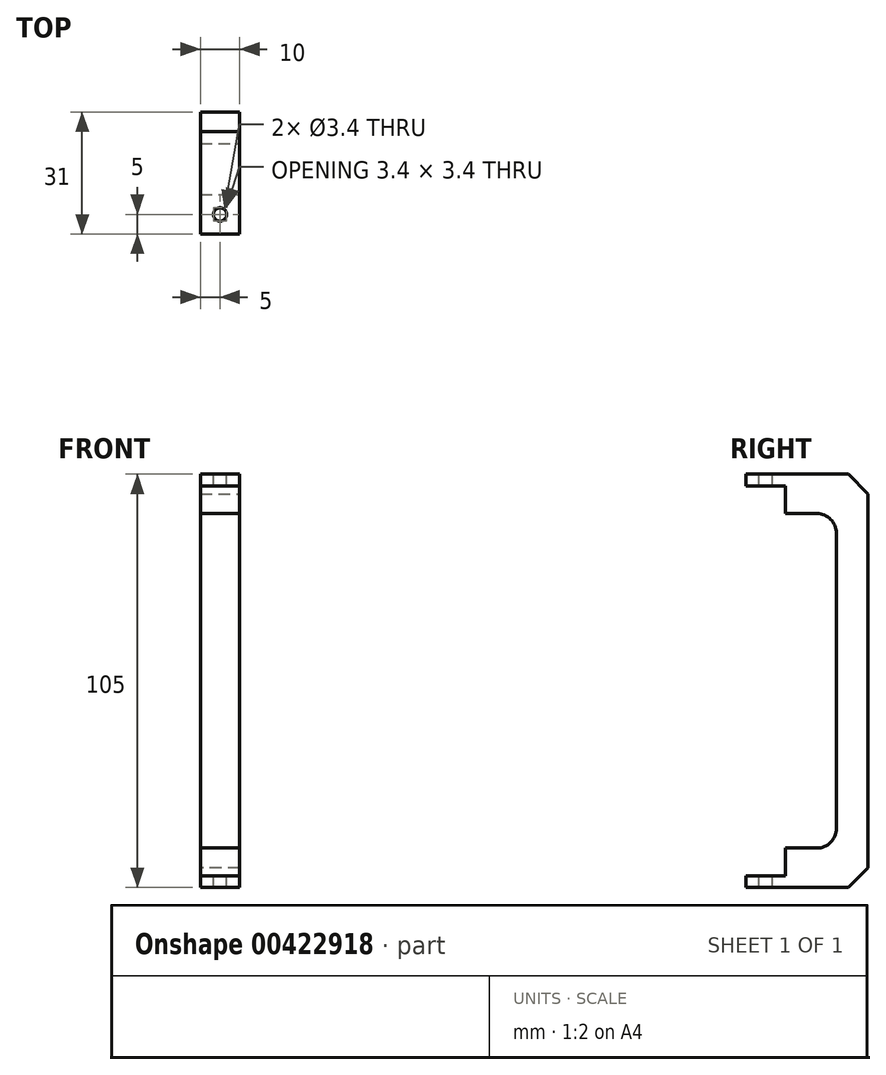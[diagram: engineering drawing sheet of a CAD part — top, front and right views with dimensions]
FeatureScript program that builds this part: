
annotation { "Feature Type Name" : "Feature", "Feature Type Description" : "" }
export const myFeature = defineFeature(function(context is Context, id is Id, definition is map)
    precondition{}
    {
        {
            var Q0;
            Q0=qCreatedBy(makeId("Right.planeOp"),FACE);
            var sketch = newSketch(context, id + "F0", { "sketchPlane" : qUnion([Q0])});
            skLineSegment(sketch, "E0.bottom", {"start": v(-15, 55) * mm, "end": v(16, 55) * mm});
            skLineSegment(sketch, "E0.top", {"start": v(-15, -50) * mm, "end": v(16, -50) * mm});
            skLineSegment(sketch, "E0.left", {"start": v(-15, 55) * mm, "end": v(-15, -50) * mm});
            skLineSegment(sketch, "E0.right", {"start": v(16, 55) * mm, "end": v(16, -50) * mm});
            skSolve(sketch);
        }
        {
            var Q0;
            Q0 = qSketchRegion(id + "F0", true);
            extrude(context, id + "F1", {"entities" : qUnion([Q0]), "depth" : 10 * mm});
        }
        {
            var Q0;
            Q0=makeQuery(id+"F1.opExtrude","CAP_FACE",FACE,{"disambiguationData":[OSD([sQuery(id+"F0.wireOp",EDGE,"E0.bottom"),sQuery(id+"F0.wireOp",EDGE,"E0.top"),sQuery(id+"F0.wireOp",EDGE,"E0.left"),sQuery(id+"F0.wireOp",EDGE,"E0.right")])],"isStart":false});
            var sketch = newSketch(context, id + "F2", { "sketchPlane" : qUnion([Q0])});
            skLineSegment(sketch, "E1.bottom", {"start": v(-25, 52) * mm, "end": v(-5, 52) * mm});
            skLineSegment(sketch, "E1.top", {"start": v(-25, -47) * mm, "end": v(-5, -47) * mm});
            skLineSegment(sketch, "E1.left", {"start": v(-25, 52) * mm, "end": v(-25, -47) * mm});
            skLineSegment(sketch, "E1.right", {"start": v(-5, 52) * mm, "end": v(-5, -47) * mm});
            skSolve(sketch);
        }
        {
            var Q0;
            Q0 = qSketchRegion(id + "F2", true);
            extrude(context, id + "F3", {"entities" : qUnion([Q0]), "operationType" : NewBodyOperationType.REMOVE, "endBound" : BoundingType.THROUGH_ALL, "oppositeDirection" : true, "depth" : 25 * mm});
        }
        {
            var Q0;
            Q0=makeQuery(id+"F1.opExtrude","CAP_FACE",FACE,{"disambiguationData":[OSD([sQuery(id+"F0.wireOp",EDGE,"E0.bottom"),sQuery(id+"F0.wireOp",EDGE,"E0.top"),sQuery(id+"F0.wireOp",EDGE,"E0.left"),sQuery(id+"F0.wireOp",EDGE,"E0.right")])],"isStart":false});
            var sketch = newSketch(context, id + "F4", { "sketchPlane" : qUnion([Q0])});
            skLineSegment(sketch, "E2.bottom", {"start": v(8, 45) * mm, "end": v(-5, 45) * mm});
            skLineSegment(sketch, "E2.top", {"start": v(8, -40) * mm, "end": v(-5, -40) * mm});
            skLineSegment(sketch, "E2.left", {"start": v(8, 45) * mm, "end": v(8, -40) * mm});
            skLineSegment(sketch, "E2.right", {"start": v(-5, 45) * mm, "end": v(-5, -40) * mm});
            skSolve(sketch);
        }
        {
            var Q0;
            Q0 = qSketchRegion(id + "F4", true);
            extrude(context, id + "F5", {"entities" : qUnion([Q0]), "operationType" : NewBodyOperationType.REMOVE, "endBound" : BoundingType.THROUGH_ALL, "oppositeDirection" : true, "depth" : 25 * mm});
        }
        {
            var Q0;
            Q0=makeQuery(id+"F1.opExtrude","SWEPT_EDGE",EDGE,{"disambiguationData":[OSD([sQuery(id+"F0.wireOp",EDGE,"E0.bottom"),sQuery(id+"F0.wireOp",EDGE,"E0.right")])]});
            var Q1;
            Q1=makeQuery(id+"F1.opExtrude","SWEPT_EDGE",EDGE,{"disambiguationData":[OSD([sQuery(id+"F0.wireOp",EDGE,"E0.top"),sQuery(id+"F0.wireOp",EDGE,"E0.right")])]});
            chamfer(context, id + "F6", {"entities" : qUnion([Q0, Q1]), "width" : 5 * mm, "tangentPropagation" : true});
        }
        {
            var Q0;
            Q0=makeQuery(id+"F1.opExtrude","SWEPT_FACE",FACE,{"disambiguationData":[OSD([sQuery(id+"F0.wireOp",EDGE,"E0.bottom")])]});
            var sketch = newSketch(context, id + "F7", { "sketchPlane" : qUnion([Q0])});
            skCircle(sketch, "E3", {"center": v(5, -10) * mm, "radius": 1.7 * mm});
            skSolve(sketch);
        }
        {
            var Q0;
            Q0 = qSketchRegion(id + "F7", true);
            extrude(context, id + "F8", {"entities" : qUnion([Q0]), "operationType" : NewBodyOperationType.REMOVE, "endBound" : BoundingType.THROUGH_ALL, "oppositeDirection" : true, "depth" : 25 * mm});
        }
        {
            var Q0;
            Q0=makeQuery(id+"F5.boolean.opBoolean","COPY",EDGE,{"derivedFrom":makeQuery(id+"F5.opExtrude","SWEPT_EDGE",EDGE,{"disambiguationData":[OSD([sQuery(id+"F4.wireOp",EDGE,"E2.bottom"),sQuery(id+"F4.wireOp",EDGE,"E2.left")])]})});
            var Q1;
            Q1=makeQuery(id+"F5.boolean.opBoolean","COPY",EDGE,{"derivedFrom":makeQuery(id+"F5.opExtrude","SWEPT_EDGE",EDGE,{"disambiguationData":[OSD([sQuery(id+"F4.wireOp",EDGE,"E2.top"),sQuery(id+"F4.wireOp",EDGE,"E2.left")])]})});
            fillet(context, id + "F9", {"entities" : qUnion([Q0, Q1]), "radius" : 5 * mm, "tangentPropagation" : true, "allowEdgeOverflow" : false});
        }
    });
